# Revit family: Indoor_Wall Lamp_Santa&Cole_TMM
name_source: partatom
category: Luminarias
revit_build: Autodesk Revit 2018 (Build: 20190510_1515(x64)
units: mm (PartAtom-declared; Revit-internal decimal feet)

## family parameters
Compartido = No
Corte con vacíos al cargar = No
Cota de conector redondo = Diámetro de uso
Número OmniClass = 23.80.70.00
Origen de luz = Sí
Punto de cálculo de habitación = No
Se basa en plano de trabajo = Sí
Siempre vertical = Sí
Tipo de pieza = Normal
Título OmniClass = Lighting

## types (4) — shared parameters
Assembly instructions - CE = https://www.santacole.com
Assembly instructions - UL = https://www.santacole.com
Cambio de temperatura de color de luz atenuada = <Ninguno>
Carga aparente = 5 VA
Elevación por defecto = 1219 mm
Energy Label = https://www.santacole.com
Fabricante = Santa & Cole
Filtro de color = 16777215
Manufacturer website = https://www.santacole.com
Modelo = TMM
Tamaño de símbolo de origen de luz = 50 mm  [stored 0.164042 ft]
Technical Information = https://www.santacole.com
URL = https://www.santacole.com
Voltaje (90-305 V) = 220 V

## per-type parameters (varying)
| type | Code | Lampshade Material | Visibility_TMM Corto | Visibility_TMM Largo |
| TMM Corto - White Parchment Lampshade | ATM3x | Santa & Cole - White Cardboard | Sí | No |
| TMM Corto - Beige Parchment Lampshade | ATM3x | Santa & Cole - Beige Cardboard | Sí | No |
| TMM Largo - White Parchment Lampshade | ATL01/ATL02 | Santa & Cole - White Cardboard | No | Sí |
| TMM Largo - Beige Parchment Lampshade | ATL01/ATL02 | Santa & Cole - Beige Cardboard | No | Sí |

note: [stored X ft] marks values corroborated as IEEE doubles in the binary element streams (Revit-internal decimal feet)
